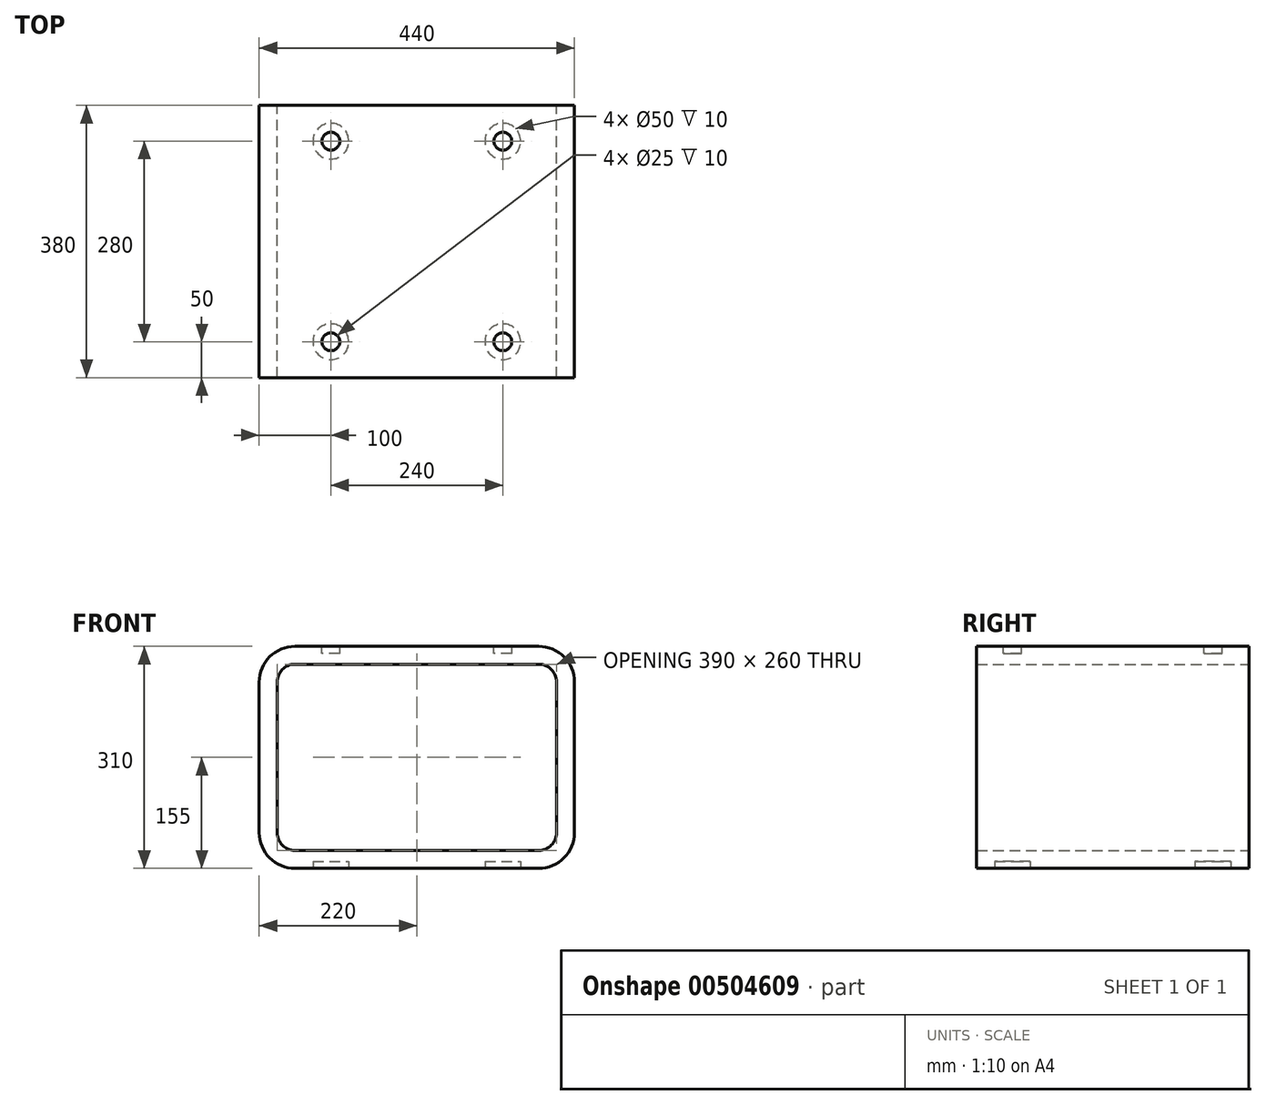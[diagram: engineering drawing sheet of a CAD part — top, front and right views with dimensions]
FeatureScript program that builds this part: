
annotation { "Feature Type Name" : "Feature", "Feature Type Description" : "" }
export const myFeature = defineFeature(function(context is Context, id is Id, definition is map)
    precondition{}
    {
        {
            var Q0;
            Q0=qCreatedBy(makeId("Front.planeOp"),FACE);
            var sketch = newSketch(context, id + "F0", { "sketchPlane" : qUnion([Q0])});
            skLineSegment(sketch, "E0", {"start": v(-170, -155) * mm, "end": v(170, -155) * mm});
            skLineSegment(sketch, "E1", {"start": v(220, 105) * mm, "end": v(220, -105) * mm});
            skLineSegment(sketch, "E2", {"start": v(170, 155) * mm, "end": v(-170, 155) * mm});
            skLineSegment(sketch, "E3", {"start": v(-220, 105) * mm, "end": v(-220, -105) * mm});
            skArc(sketch, "E4", {"start": v(170, -155) * mm, "mid": v(205.36, -140.36) * mm, "end": v(220, -105) * mm});
            skArc(sketch, "E5", {"start": v(220, 105) * mm, "mid": v(205.36, 140.36) * mm, "end": v(170, 155) * mm});
            skArc(sketch, "E6", {"start": v(-170, 155) * mm, "mid": v(-205.36, 140.36) * mm, "end": v(-220, 105) * mm});
            skArc(sketch, "E7", {"start": v(-220, -105) * mm, "mid": v(-205.36, -140.36) * mm, "end": v(-170, -155) * mm});
            skLineSegment(sketch, "E8.bottom", {"start": v(170, -130) * mm, "end": v(-170, -130) * mm});
            skLineSegment(sketch, "E8.top", {"start": v(170, 130) * mm, "end": v(-170, 130) * mm});
            skLineSegment(sketch, "E8.left", {"start": v(195, -105) * mm, "end": v(195, 105) * mm});
            skLineSegment(sketch, "E8.right", {"start": v(-195, -105) * mm, "end": v(-195, 105) * mm});
            skPoint(sketch, "E8.middle", {"position": v(0, 0) * mm});
            skPoint(sketch, "E9.visualSharp", {"position": v(195, 130) * mm});
            skArc(sketch, "E9.filletArc", {"start": v(195, 105) * mm, "mid": v(187.68, 122.68) * mm, "end": v(170, 130) * mm});
            skPoint(sketch, "E10.visualSharp", {"position": v(-195, 130) * mm});
            skArc(sketch, "E10.filletArc", {"start": v(-170, 130) * mm, "mid": v(-187.68, 122.68) * mm, "end": v(-195, 105) * mm});
            skPoint(sketch, "E11.visualSharp", {"position": v(-195, -130) * mm});
            skArc(sketch, "E11.filletArc", {"start": v(-195, -105) * mm, "mid": v(-187.68, -122.68) * mm, "end": v(-170, -130) * mm});
            skPoint(sketch, "E12.visualSharp", {"position": v(195, -130) * mm});
            skArc(sketch, "E12.filletArc", {"start": v(170, -130) * mm, "mid": v(187.68, -122.68) * mm, "end": v(195, -105) * mm});
            skSolve(sketch);
        }
        {
            var Q0;
            Q0=makeQuery(id+"F0.imprint","IMPRINT",FACE,{"disambiguationData":[TD([[makeQuery(id+"F0.imprint","IMPRINT",EDGE,{"derivedFrom":sQuery(id+"F0.wireOp",EDGE,"E0")}),1.0]])]});
            extrude(context, id + "F1", {"entities" : qUnion([Q0]), "depth" : 380 * mm});
        }
        {
            var Q0;
            Q0=makeQuery(id+"F1.opExtrude","SWEPT_FACE",FACE,{"disambiguationData":[OSD([sQuery(id+"F0.wireOp",EDGE,"E0")])]});
            var sketch = newSketch(context, id + "F2", { "sketchPlane" : qUnion([Q0])});
            skCircle(sketch, "E13", {"center": v(-120, 330) * mm, "radius": 25 * mm});
            skCircle(sketch, "E14", {"center": v(-120, 50) * mm, "radius": 25 * mm});
            skCircle(sketch, "E15", {"center": v(120, 50) * mm, "radius": 25 * mm});
            skCircle(sketch, "E16", {"center": v(120, 330) * mm, "radius": 25 * mm});
            skSolve(sketch);
        }
        {
            var Q0;
            Q0=makeQuery(id+"F2.imprint","IMPRINT",FACE,{"disambiguationData":[TD([[makeQuery(id+"F2.imprint","IMPRINT",EDGE,{"derivedFrom":sQuery(id+"F2.wireOp",EDGE,"E14")}),1.0]])]});
            var Q1;
            Q1=makeQuery(id+"F2.imprint","IMPRINT",FACE,{"disambiguationData":[TD([[makeQuery(id+"F2.imprint","IMPRINT",EDGE,{"derivedFrom":sQuery(id+"F2.wireOp",EDGE,"E13")}),1.0]])]});
            var Q2;
            Q2=makeQuery(id+"F2.imprint","IMPRINT",FACE,{"disambiguationData":[TD([[makeQuery(id+"F2.imprint","IMPRINT",EDGE,{"derivedFrom":sQuery(id+"F2.wireOp",EDGE,"E15")}),1.0]])]});
            var Q3;
            Q3=makeQuery(id+"F2.imprint","IMPRINT",FACE,{"disambiguationData":[TD([[makeQuery(id+"F2.imprint","IMPRINT",EDGE,{"derivedFrom":sQuery(id+"F2.wireOp",EDGE,"E16")}),1.0]])]});
            extrude(context, id + "F3", {"entities" : qUnion([Q0, Q1, Q2, Q3]), "operationType" : NewBodyOperationType.REMOVE, "oppositeDirection" : true, "depth" : 10 * mm});
        }
        {
            var Q0;
            Q0=makeQuery(id+"F1.opExtrude","SWEPT_FACE",FACE,{"disambiguationData":[OSD([sQuery(id+"F0.wireOp",EDGE,"E2")])]});
            var sketch = newSketch(context, id + "F4", { "sketchPlane" : qUnion([Q0])});
            skCircle(sketch, "E17", {"center": v(-120, -50) * mm, "radius": 12.5 * mm});
            skCircle(sketch, "E18", {"center": v(-120, -330) * mm, "radius": 12.5 * mm});
            skCircle(sketch, "E19", {"center": v(120, -330) * mm, "radius": 12.5 * mm});
            skCircle(sketch, "E20", {"center": v(120, -50) * mm, "radius": 12.5 * mm});
            skSolve(sketch);
        }
        {
            var Q0;
            Q0=makeQuery(id+"F4.imprint","IMPRINT",FACE,{"disambiguationData":[TD([[makeQuery(id+"F4.imprint","IMPRINT",EDGE,{"derivedFrom":sQuery(id+"F4.wireOp",EDGE,"E17")}),1.0]])]});
            var Q1;
            Q1=makeQuery(id+"F4.imprint","IMPRINT",FACE,{"disambiguationData":[TD([[makeQuery(id+"F4.imprint","IMPRINT",EDGE,{"derivedFrom":sQuery(id+"F4.wireOp",EDGE,"E18")}),1.0]])]});
            var Q2;
            Q2=makeQuery(id+"F4.imprint","IMPRINT",FACE,{"disambiguationData":[TD([[makeQuery(id+"F4.imprint","IMPRINT",EDGE,{"derivedFrom":sQuery(id+"F4.wireOp",EDGE,"E19")}),1.0]])]});
            var Q3;
            Q3=makeQuery(id+"F4.imprint","IMPRINT",FACE,{"disambiguationData":[TD([[makeQuery(id+"F4.imprint","IMPRINT",EDGE,{"derivedFrom":sQuery(id+"F4.wireOp",EDGE,"E20")}),1.0]])]});
            extrude(context, id + "F5", {"entities" : qUnion([Q0, Q1, Q2, Q3]), "operationType" : NewBodyOperationType.REMOVE, "oppositeDirection" : true, "depth" : 10 * mm});
        }
    });
